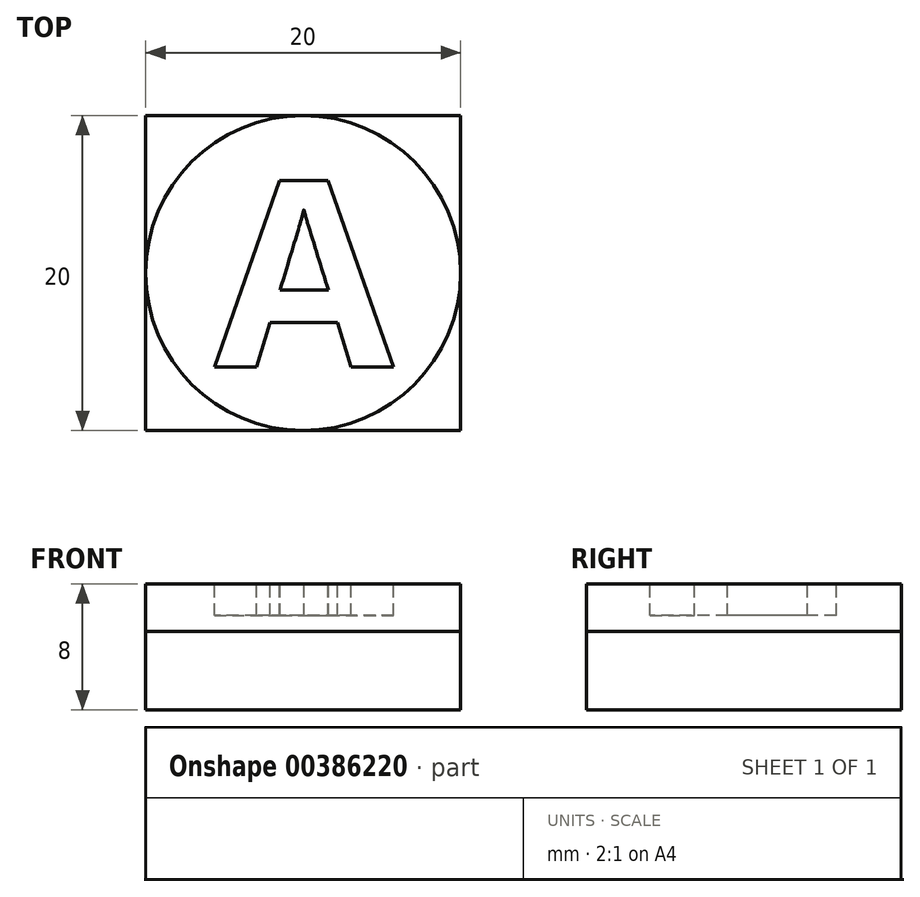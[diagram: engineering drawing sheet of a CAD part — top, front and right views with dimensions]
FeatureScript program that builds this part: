
annotation { "Feature Type Name" : "Feature", "Feature Type Description" : "" }
export const myFeature = defineFeature(function(context is Context, id is Id, definition is map)
    precondition{}
    {
        {
            var Q0;
            Q0=qCreatedBy(makeId("Top.planeOp"),FACE);
            var sketch = newSketch(context, id + "F0", { "sketchPlane" : qUnion([Q0])});
            skLineSegment(sketch, "E0.bottom", {"start": v(10, -10) * mm, "end": v(-10, -10) * mm});
            skLineSegment(sketch, "E0.top", {"start": v(10, 10) * mm, "end": v(-10, 10) * mm});
            skLineSegment(sketch, "E0.left", {"start": v(10, -10) * mm, "end": v(10, 10) * mm});
            skLineSegment(sketch, "E0.right", {"start": v(-10, -10) * mm, "end": v(-10, 10) * mm});
            skPoint(sketch, "E0.middle", {"position": v(0, 0) * mm});
            skSolve(sketch);
        }
        {
            var Q0;
            Q0 = qSketchRegion(id + "F0", true);
            extrude(context, id + "F1", {"entities" : qUnion([Q0]), "depth" : 5 * mm, "offsetDistance" : 25 * mm});
        }
        {
            var Q0;
            Q0=makeQuery(id+"F1.opExtrude","CAP_FACE",FACE,{"disambiguationData":[OSD([sQuery(id+"F0.wireOp",EDGE,"E0.bottom"),sQuery(id+"F0.wireOp",EDGE,"E0.top"),sQuery(id+"F0.wireOp",EDGE,"E0.left"),sQuery(id+"F0.wireOp",EDGE,"E0.right")])],"isStart":false});
            var sketch = newSketch(context, id + "F2", { "sketchPlane" : qUnion([Q0])});
            skCircle(sketch, "E1", {"center": v(0, 0) * mm, "radius": 10 * mm});
            skSolve(sketch);
        }
        {
            var Q0;
            Q0 = qSketchRegion(id + "F2", true);
            extrude(context, id + "F3", {"entities" : qUnion([Q0]), "operationType" : NewBodyOperationType.ADD, "depth" : 3 * mm, "offsetDistance" : 25 * mm});
        }
        {
            var Q0;
            Q0=makeQuery(id+"F3.opExtrude","CAP_FACE",FACE,{"disambiguationData":[OSD([sQuery(id+"F2.wireOp",EDGE,"E1")])],"isStart":false});
            var sketch = newSketch(context, id + "F4", { "sketchPlane" : qUnion([Q0])});
            skText(sketch, "E2", { "text": "A", "fontName": "OpenSans-Bold.ttf"});
            skPoint(sketch, "E3", {"position": v(0.59, -0.02) * mm});
            const initialGuessF4  = {"E2": [-0.00564, -0.00596, 1, 0, 0.01187]};
            skSetInitialGuess(sketch, initialGuessF4);
            skSolve(sketch);
        }
        {
            var Q0;
            Q0 = qSketchRegion(id + "F4", true);
            extrude(context, id + "F5", {"entities" : qUnion([Q0]), "operationType" : NewBodyOperationType.REMOVE, "oppositeDirection" : true, "depth" : 2 * mm, "offsetDistance" : 25 * mm});
        }
    });
